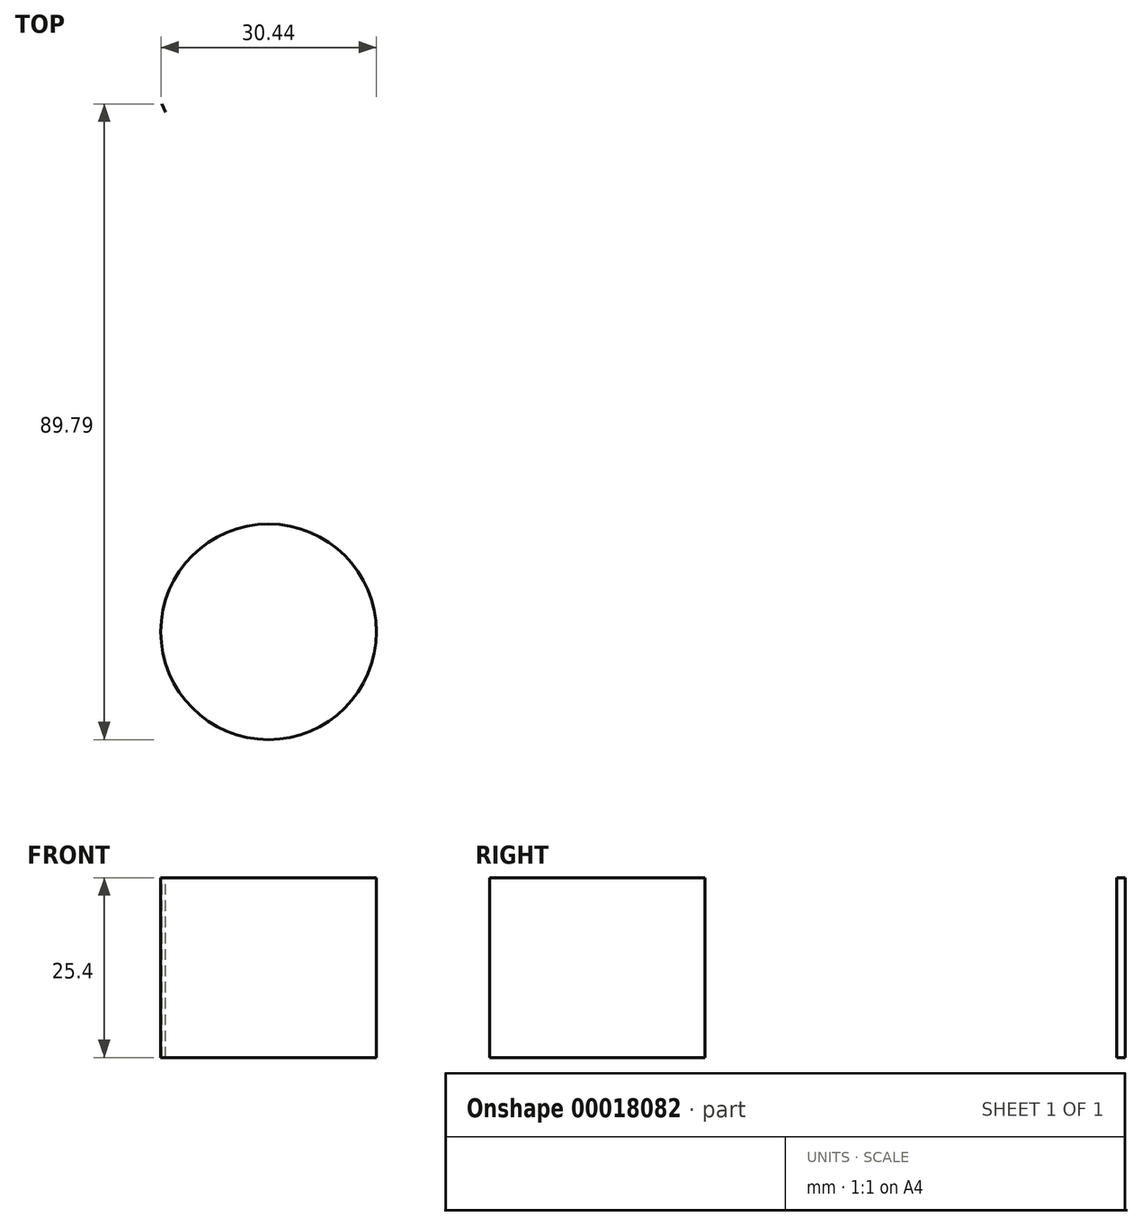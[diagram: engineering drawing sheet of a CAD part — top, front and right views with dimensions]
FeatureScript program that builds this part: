
annotation { "Feature Type Name" : "Feature", "Feature Type Description" : "" }
export const myFeature = defineFeature(function(context is Context, id is Id, definition is map)
    precondition{}
    {
        {
            var Q0;
            Q0=qCreatedBy(makeId("Top.planeOp"),FACE);
            var sketch = newSketch(context, id + "F0", { "sketchPlane" : qUnion([Q0])});
            skCircle(sketch, "E0", {"center": v(-116.89, -71.7) * mm, "radius": 19.33 * mm});
            skCircle(sketch, "E1", {"center": v(-84.27, -138.13) * mm, "radius": 15.22 * mm});
            skLineSegment(sketch, "E2", {"start": v(-99.35, -63.56) * mm, "end": v(-70.26, -132.19) * mm});
            skLineSegment(sketch, "E3", {"start": v(-134.6, -79.42) * mm, "end": v(-97.55, -145.57) * mm});
            skSolve(sketch);
        }
        {
            var Q0;
            {var subQ0=sQuery(id+"F0.wireOp",EDGE,"E1");var subQ2=makeQuery(id+"F0.imprint","INTERSECT",VERTEX,{"derivedFrom":[subQ0,sQuery(id+"F0.wireOp",EDGE,"E2")]});Q0=makeQuery(id+"F0.imprint","IMPRINT",FACE,{"disambiguationData":[TD([[makeQuery(id+"F0.imprint","IMPRINT",EDGE,{"disambiguationData":[TD([[subQ2,-1.0]])],"derivedFrom":subQ0}),1.0]])]});}
            var Q1;
            {var subQ1=sQuery(id+"F0.wireOp",EDGE,"E0");var subQ5=sQuery(id+"F0.wireOp",EDGE,"E2");var subQ6=makeQuery(id+"F0.imprint","INTERSECT",VERTEX,{"disambiguationData":[OD(1.0)],"derivedFrom":[subQ1,subQ5]});Q1=makeQuery(id+"F0.imprint","IMPRINT",FACE,{"disambiguationData":[TD([[makeQuery(id+"F0.imprint","IMPRINT",EDGE,{"disambiguationData":[TD([[subQ6,1.0]])],"derivedFrom":subQ1}),-1.0]])]});}
            var Q2;
            {var subQ1=sQuery(id+"F0.wireOp",EDGE,"E0");var subQ4=sQuery(id+"F0.wireOp",EDGE,"E2");var subQ6=makeQuery(id+"F0.imprint","INTERSECT",VERTEX,{"disambiguationData":[OD(0.0)],"derivedFrom":[subQ1,subQ4]});Q2=makeQuery(id+"F0.imprint","IMPRINT",FACE,{"disambiguationData":[TD([[makeQuery(id+"F0.imprint","IMPRINT",EDGE,{"disambiguationData":[TD([[subQ6,-1.0]])],"derivedFrom":subQ1}),1.0]])]});}
            var Q3;
            Q3=sQuery(id+"F0.wireOp",EDGE,"E3");
            var Q4;
            Q4=sQuery(id+"F0.wireOp",EDGE,"E2");
            var Q5;
            Q5=sQuery(id+"F0.wireOp",EDGE,"E1");
            var Q6;
            Q6=sQuery(id+"F0.wireOp",EDGE,"E0");
            extrude(context, id + "F1", {"entities" : qUnion([Q0, Q1, Q2]), "surfaceEntities" : qUnion([Q3, Q4, Q5, Q6]), "oppositeDirection" : true, "depth" : 25.4 * mm});
        }
    });
